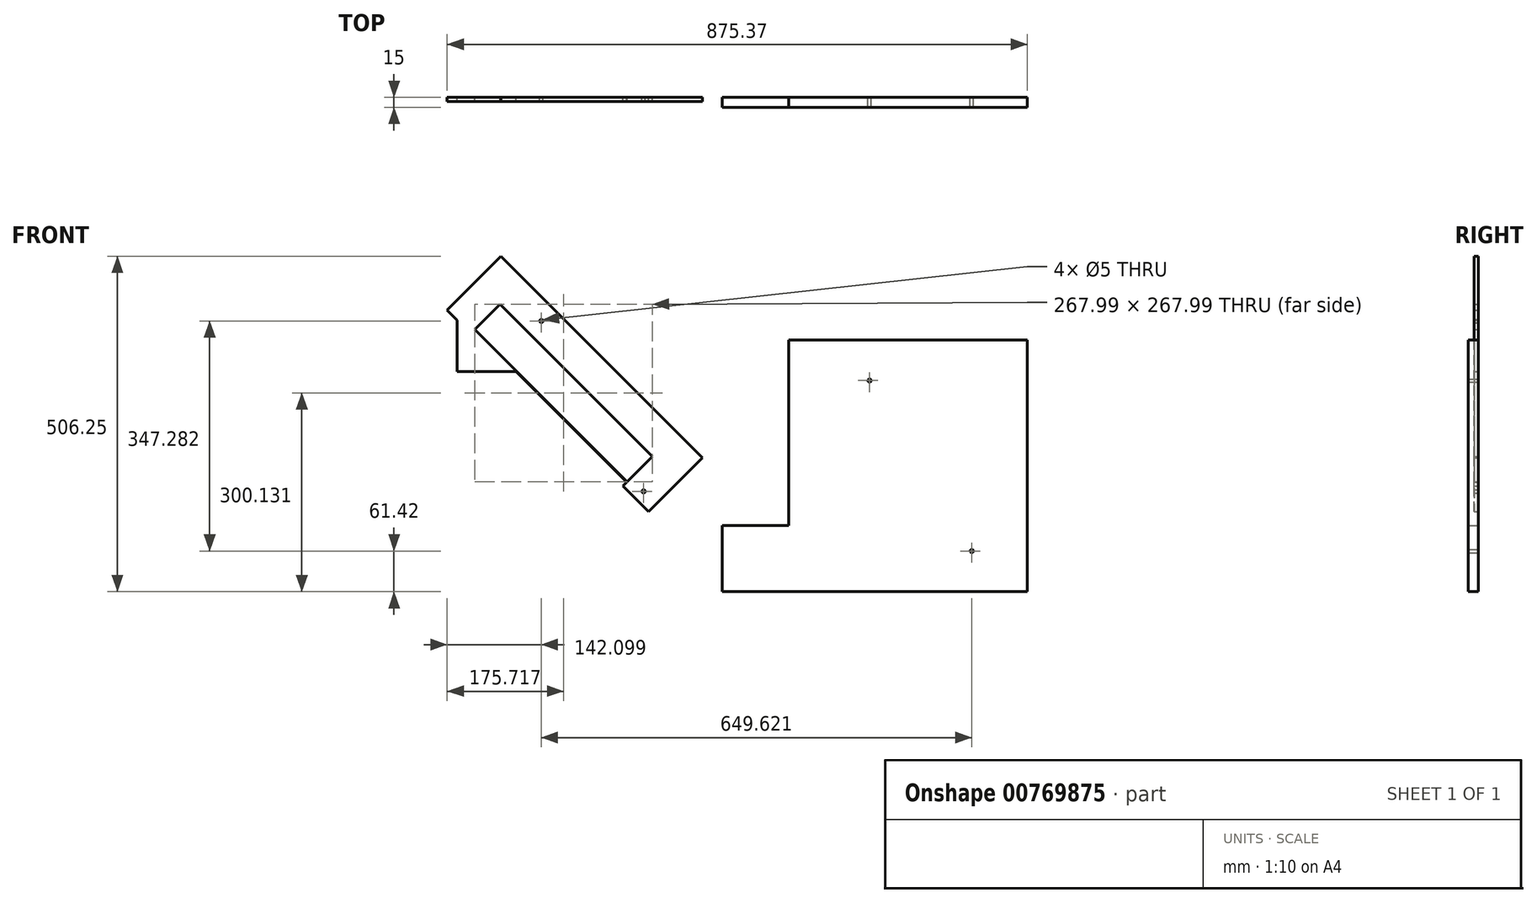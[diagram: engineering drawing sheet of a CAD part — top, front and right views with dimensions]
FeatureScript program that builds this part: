
annotation { "Feature Type Name" : "Feature", "Feature Type Description" : "" }
export const myFeature = defineFeature(function(context is Context, id is Id, definition is map)
    precondition{}
    {
        {
            var Q0;
            Q0=qCreatedBy(makeId("Front.planeOp"),FACE);
            var sketch = newSketch(context, id + "F0", { "sketchPlane" : qUnion([Q0])});
            skLineSegment(sketch, "E0", {"start": v(0, 0) * mm, "end": v(-300, 0) * mm, "construction": true});
            skLineSegment(sketch, "E1", {"start": v(0, 0) * mm, "end": v(0, 100) * mm, "construction": true});
            skLineSegment(sketch, "E2", {"start": v(0, 100) * mm, "end": v(-300, 100) * mm, "construction": true});
            skLineSegment(sketch, "E3", {"start": v(0, 40) * mm, "end": v(-300, 40) * mm, "construction": true});
            skLineSegment(sketch, "E4", {"start": v(0, 35) * mm, "end": v(-300, 35) * mm, "construction": true});
            skLineSegment(sketch, "E5", {"start": v(0, 14) * mm, "end": v(-300, 14) * mm, "construction": true});
            skLineSegment(sketch, "E6", {"start": v(0, 40) * mm, "end": v(-60, 100) * mm, "construction": true});
            skLineSegment(sketch, "E7", {"start": v(0, 14) * mm, "end": v(-21, 35) * mm, "construction": true});
            skLineSegment(sketch, "E8", {"start": v(-60, 100) * mm, "end": v(-21, 35) * mm, "construction": true});
            skLineSegment(sketch, "E9", {"start": v(-40.5, 67.5) * mm, "end": v(83.95, 142.17) * mm, "construction": true});
            skLineSegment(sketch, "E10", {"start": v(-60, 100) * mm, "end": v(83.95, 142.17) * mm, "construction": true});
            skLineSegment(sketch, "E11", {"start": v(-123.04, 163.04) * mm, "end": v(106.77, -66.77) * mm});
            skLineSegment(sketch, "E12", {"start": v(-123.04, 163.04) * mm, "end": v(-128.7, 157.38) * mm});
            skLineSegment(sketch, "E13", {"start": v(-128.7, 157.38) * mm, "end": v(-164.05, 192.74) * mm});
            skLineSegment(sketch, "E14", {"start": v(-164.05, 192.74) * mm, "end": v(-82.73, 274.05) * mm});
            skLineSegment(sketch, "E15", {"start": v(-82.73, 274.05) * mm, "end": v(221.32, -30) * mm});
            skLineSegment(sketch, "E16", {"start": v(221.32, -30) * mm, "end": v(140, -111.32) * mm});
            skLineSegment(sketch, "E17", {"start": v(140, -111.32) * mm, "end": v(101.12, -72.43) * mm});
            skLineSegment(sketch, "E18", {"start": v(101.12, -72.43) * mm, "end": v(145.66, -27.88) * mm});
            skLineSegment(sketch, "E19", {"start": v(145.66, -27.88) * mm, "end": v(-84.15, 201.93) * mm});
            skLineSegment(sketch, "E20", {"start": v(-84.15, 201.93) * mm, "end": v(-123.04, 163.04) * mm});
            skLineSegment(sketch, "E21", {"start": v(-122.33, 163.74) * mm, "end": v(107.48, -66.07) * mm});
            skLineSegment(sketch, "E22", {"start": v(-21.95, 176.5) * mm, "end": v(132.4, -80.75) * mm, "construction": true});
            skCircle(sketch, "E23", {"center": v(-21.95, 176.5) * mm, "radius": 2.5 * mm});
            skCircle(sketch, "E24", {"center": v(132.4, -80.75) * mm, "radius": 2.5 * mm});
            skLineSegment(sketch, "E25", {"start": v(-21.95, 176.5) * mm, "end": v(122, 218.67) * mm, "construction": true});
            skLineSegment(sketch, "E26", {"start": v(132.4, -80.75) * mm, "end": v(276.35, -38.58) * mm, "construction": true});
            skLineSegment(sketch, "E27", {"start": v(351.32, 147.8) * mm, "end": v(351.32, -132.2) * mm});
            skLineSegment(sketch, "E28", {"start": v(351.32, -132.2) * mm, "end": v(251.32, -132.2) * mm});
            skLineSegment(sketch, "E29", {"start": v(351.32, 147.8) * mm, "end": v(711.32, 147.8) * mm});
            skLineSegment(sketch, "E30", {"start": v(711.32, 147.8) * mm, "end": v(711.32, -232.2) * mm});
            skLineSegment(sketch, "E31", {"start": v(711.32, -232.2) * mm, "end": v(251.32, -232.2) * mm});
            skLineSegment(sketch, "E32", {"start": v(251.32, -232.2) * mm, "end": v(251.32, -132.2) * mm});
            skLineSegment(sketch, "E33", {"start": v(122, 218.67) * mm, "end": v(276.35, -38.58) * mm, "construction": true});
            skLineSegment(sketch, "E34", {"start": v(473.32, 86.47) * mm, "end": v(627.67, -170.78) * mm, "construction": true});
            skCircle(sketch, "E35", {"center": v(473.32, 86.47) * mm, "radius": 2.5 * mm});
            skCircle(sketch, "E36", {"center": v(627.67, -170.78) * mm, "radius": 2.5 * mm});
            skLineSegment(sketch, "E37", {"start": v(-60, 100) * mm, "end": v(-60, 177.78) * mm});
            skLineSegment(sketch, "E38", {"start": v(-60, 177.78) * mm, "end": v(-149.1, 177.78) * mm});
            skLineSegment(sketch, "E39", {"start": v(-149.1, 177.78) * mm, "end": v(-149.1, 100) * mm});
            skLineSegment(sketch, "E40", {"start": v(-149.1, 100) * mm, "end": v(-60, 100) * mm});
            skSolve(sketch);
        }
        {
            var Q0;
            {var subQ7=sQuery(id+"F0.wireOp",EDGE,"E12");Q0=makeQuery(id+"F0.imprint","IMPRINT",FACE,{"disambiguationData":[TD([[makeQuery(id+"F0.imprint","IMPRINT",EDGE,{"derivedFrom":subQ7}),-1.0]])]});}
            var Q1;
            {var subQ0=sQuery(id+"F0.wireOp",EDGE,"E11");Q1=makeQuery(id+"F0.imprint","IMPRINT",FACE,{"disambiguationData":[TD([[makeQuery(id+"F0.imprint","IMPRINT",EDGE,{"derivedFrom":subQ0}),1.0]])]});}
            var Q2;
            {var subQ13=sQuery(id+"F0.wireOp",EDGE,"E14");Q2=makeQuery(id+"F0.imprint","IMPRINT",FACE,{"disambiguationData":[TD([[makeQuery(id+"F0.imprint","IMPRINT",EDGE,{"derivedFrom":subQ13}),-1.0]])]});}
            var Q3;
            {var subQ1=sQuery(id+"F0.wireOp",EDGE,"E12");Q3=makeQuery(id+"F0.imprint","IMPRINT",FACE,{"disambiguationData":[TD([[makeQuery(id+"F0.imprint","IMPRINT",EDGE,{"derivedFrom":subQ1}),1.0]])]});}
            extrude(context, id + "F1", {"entities" : qUnion([Q0, Q1, Q2, Q3]), "depth" : 6 * mm, "offsetDistance" : 25 * mm});
        }
        {
            var Q0;
            Q0=makeQuery(id+"F0.imprint","IMPRINT",FACE,{"disambiguationData":[TD([[makeQuery(id+"F0.imprint","IMPRINT",EDGE,{"derivedFrom":sQuery(id+"F0.wireOp",EDGE,"E27")}),1.0]])]});
            extrude(context, id + "F2", {"entities" : qUnion([Q0]), "depth" : 15 * mm, "offsetDistance" : 25 * mm});
        }
    });
